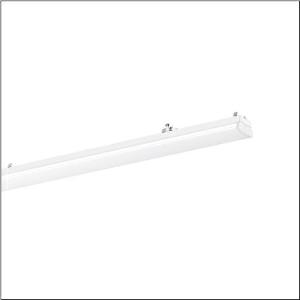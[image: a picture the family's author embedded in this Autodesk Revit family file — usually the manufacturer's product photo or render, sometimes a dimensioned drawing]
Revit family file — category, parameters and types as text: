
# Revit family: licross_r__11_recessed_opal_mo_51tl1ddv44xg_44fd
name_source: partatom
category: Lighting Fixtures
units: mm (PartAtom-declared; Revit-internal decimal feet)

## family parameters
Cut with Voids When Loaded = No
Host = Face
Light Source = No
Part Type = Normal
Room Calculation Point = No
Round Connector Dimension = Use Diameter
Shared = No

## types (1)
- --- (1 x LED, 4120 lm, 22.3 W, 4000K)
    Apparent Load = 22 VA
    CIE Flux Codes = 44 73 91 87 100
    Color Rendering = 80
    Color Temperature = 4000K
    Default Elevation = 1800 mm
    Description = Licross® 11 recessed opal MO, luminaire insert, of sheet steel, coil coated, white, length: 2.250mm, width: 76mm, height: 87mm, LED rated luminous flux: 4.120lm, light colour: 840, control gear: DALI 2, with plug, 5-pole, with phase selection, mains connection: 220..240V, AC, 50/60Hz, rated input power: 22W, halogen-free wiring, primary optical cover: cover, of PMMA, light emission: direct with ceiling illumination distribution, primary light characteristic: symmetric, protection rating (complete): IP40, insulation class (complete): insulation class I (protective earthing), certification: CE, ENEC, VDE, UKCA, protection symbol: D if used in an environment without relevant dust loads with corresponding accessories, impact resistance: IK06, permissible ambient temperature for indoor applications: -25..+45°C, corresponds to IFS (International Featured Standards) requirements for safety and quality in the food industry, reducing of maximum allowable ambient temperature of 5°C with ceiling mounting, LABS conformity tested according to VDMA 24364:2018-05, packaging unit: 1 piece
    Height = 83 mm
    Lamp = 1 x LED
    Lamp Light Flux = 4120 lm
    Lamp Power = 22.3 W
    Lamp count = 1
    Length = 2250 mm
    Luminous efficacy = 185 lm/W
    Manufacturer = Siteco
    ModVariant = No
    Model = 51TL1DDV44XG
    Mounting Place = Ceiling
    Mounting Type = Pendant
    Number of Poles = 1
    OnlyDefault = Yes
    Power Factor = 1
    Product Name = Licross® 11 recessed opal MO
    Product group = luminaire insert
    ProductGroupID = 901
    Protection Class = Protection class I
    Protection Degree = IP 40
    RLX_Detail_Level = 1
    RLX_Emergency_Light_Flux = 0 lm
    RLX_Emergency_Type = 0
    RLX_Emergency_Type_DB = No
    RlxData = <blob elided: 17717 chars, md5=fbbfdd12>
    Socket = socket
    Standby Power = 0 W
    System Light Flux = 4120 lm
    System Power = 22 W
    Type Comments = factory setting: luminous flux: 100 % | dim-lin: 254 | 100 mA
    Type Image = l_1313666.jpg
    URL = http://relux.com
    VarID = @adj_027669
    Voltage = 0 V
    Weight = 0.00 kg
    Width = 76 mm

## geometry (parser evidence)
native form markers: Blend x4, Sweep x11
no freeform markers — native parametric forms only
